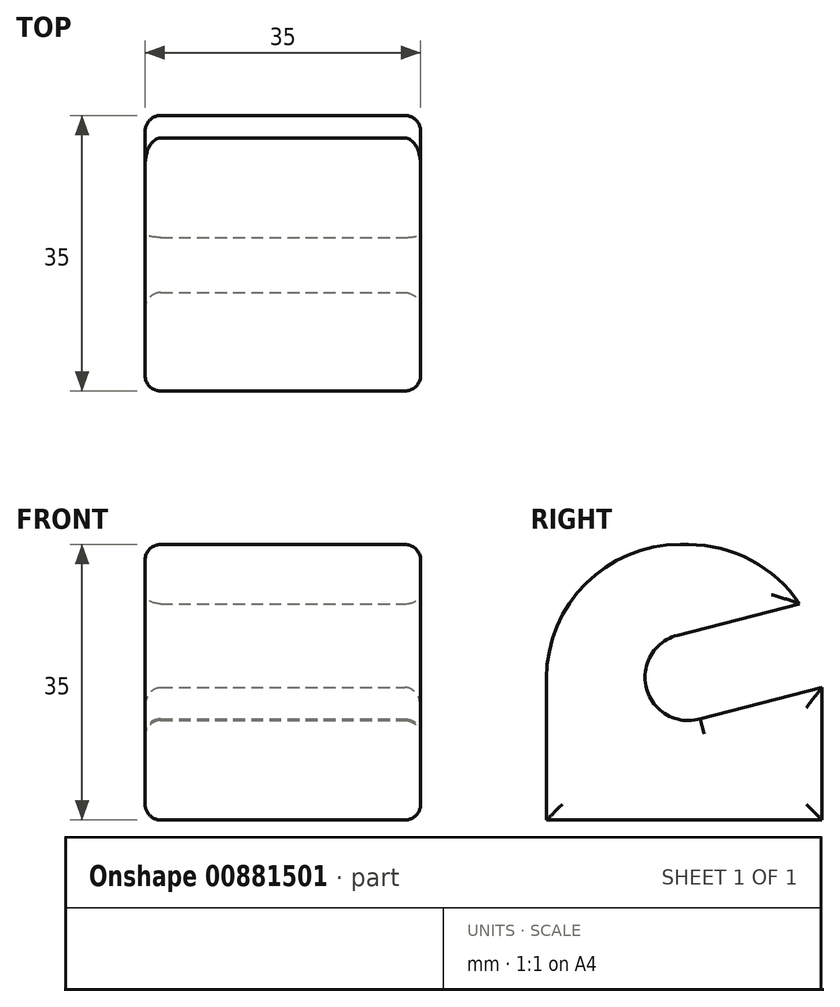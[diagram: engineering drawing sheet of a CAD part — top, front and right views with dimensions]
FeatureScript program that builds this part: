
annotation { "Feature Type Name" : "Feature", "Feature Type Description" : "" }
export const myFeature = defineFeature(function(context is Context, id is Id, definition is map)
    precondition{}
    {
        {
            var Q0;
            Q0=qCreatedBy(makeId("Top.planeOp"),FACE);
            var sketch = newSketch(context, id + "F0", { "sketchPlane" : qUnion([Q0])});
            skLineSegment(sketch, "E0.bottom", {"start": v(17.5, 17.5) * mm, "end": v(-17.5, 17.5) * mm});
            skLineSegment(sketch, "E0.top", {"start": v(17.5, -17.5) * mm, "end": v(-17.5, -17.5) * mm});
            skLineSegment(sketch, "E0.left", {"start": v(17.5, 17.5) * mm, "end": v(17.5, -17.5) * mm});
            skLineSegment(sketch, "E0.right", {"start": v(-17.5, 17.5) * mm, "end": v(-17.5, -17.5) * mm});
            skPoint(sketch, "E0.middle", {"position": v(0, 0) * mm});
            skPoint(sketch, "E1.visualSharp", {"position": v(-17.5, 17.5) * mm});
            skLineSegment(sketch, "E1.filletArc", {"start": v(-17.5, 17.5) * mm, "end": v(-17.5, 17.5) * mm});
            skPoint(sketch, "E2.visualSharp", {"position": v(17.5, 17.5) * mm});
            skLineSegment(sketch, "E2.filletArc", {"start": v(17.5, 17.5) * mm, "end": v(17.5, 17.5) * mm});
            skPoint(sketch, "E3.visualSharp", {"position": v(17.5, -17.5) * mm});
            skLineSegment(sketch, "E3.filletArc", {"start": v(17.5, -17.5) * mm, "end": v(17.5, -17.5) * mm});
            skPoint(sketch, "E4.visualSharp", {"position": v(-17.5, -17.5) * mm});
            skLineSegment(sketch, "E4.filletArc", {"start": v(-17.5, -17.5) * mm, "end": v(-17.5, -17.5) * mm});
            skSolve(sketch);
        }
        {
            var Q0;
            Q0=makeQuery(id+"F0.imprint","IMPRINT",FACE,{"disambiguationData":[TD([[makeQuery(id+"F0.imprint","IMPRINT",EDGE,{"derivedFrom":sQuery(id+"F0.wireOp",EDGE,"E0.bottom")}),1.0]])]});
            extrude(context, id + "F1", {"entities" : qUnion([Q0]), "depth" : 35 * mm, "offsetDistance" : 25 * mm});
        }
        {
            var Q0;
            Q0=makeQuery(id+"F1.opExtrude","CAP_EDGE",EDGE,{"disambiguationData":[OSD([sQuery(id+"F0.wireOp",EDGE,"E0.top")])],"isStart":false});
            var Q1;
            Q1=makeQuery(id+"F1.opExtrude","CAP_EDGE",EDGE,{"disambiguationData":[OSD([sQuery(id+"F0.wireOp",EDGE,"E0.bottom")])],"isStart":false});
            fillet(context, id + "F2", {"entities" : qUnion([Q0, Q1]), "radius" : 17 * mm, "allowEdgeOverflow" : false});
        }
        {
            var Q0;
            Q0=makeQuery(id+"F1.opExtrude","SWEPT_FACE",FACE,{"disambiguationData":[OSD([sQuery(id+"F0.wireOp",EDGE,"E0.left")])]});
            var sketch = newSketch(context, id + "F3", { "sketchPlane" : qUnion([Q0])});
            skSolve(sketch);
        }
        {
            var Q0;
            {var subQ0=sQuery(id+"F0.wireOp",EDGE,"E0.left");Q0=makeQuery(id+"F3.imprint","IMPRINT",FACE,{"disambiguationData":[TD([[makeQuery(id+"F3.imprint","IMPRINT",EDGE,{"derivedFrom":makeQuery(id+"F1.opExtrude","CAP_EDGE",EDGE,{"disambiguationData":[OSD([subQ0])],"isStart":true})}),-1.0]])]});}
            var sketch = newSketch(context, id + "F4", { "sketchPlane" : qUnion([Q0])});
            skLineSegment(sketch, "E5", {"start": v(14.62, 27.47) * mm, "end": v(-0.87, 23.47) * mm});
            skLineSegment(sketch, "E6", {"start": v(17.5, 16.85) * mm, "end": v(2, 12.85) * mm});
            skArc(sketch, "E7", {"start": v(-0.87, 23.47) * mm, "mid": v(-4.8, 16.7) * mm, "end": v(2, 12.85) * mm});
            skSolve(sketch);
        }
        {
            var Q0;
            Q0 = qSketchRegion(id + "F3", true);
            var Q1;
            {var subQ6=sQuery(id+"F4.wireOp",EDGE,"E5");Q1=makeQuery(id+"F4.imprint","IMPRINT",FACE,{"disambiguationData":[TD([[makeQuery(id+"F4.imprint","IMPRINT",EDGE,{"derivedFrom":subQ6}),1.0]])]});}
            extrude(context, id + "F5", {"entities" : qUnion([Q0, Q1]), "operationType" : NewBodyOperationType.REMOVE, "endBound" : BoundingType.THROUGH_ALL, "oppositeDirection" : true, "depth" : 25 * mm, "offsetDistance" : 25 * mm});
        }
        {
            var Q0;
            Q0=makeQuery(id+"F1.opExtrude","SWEPT_FACE",FACE,{"disambiguationData":[OSD([sQuery(id+"F0.wireOp",EDGE,"E0.left")])]});
            var Q1;
            Q1=makeQuery(id+"F1.opExtrude","SWEPT_FACE",FACE,{"disambiguationData":[OSD([sQuery(id+"F0.wireOp",EDGE,"E0.right")])]});
            var Q2;
            Q2=makeQuery(id+"F5.boolean.opBoolean","COPY",EDGE,{"derivedFrom":makeQuery(id+"F5.opExtrude","SWEPT_EDGE",EDGE,{"disambiguationData":[OSD([sQuery(id+"F0.wireOp",EDGE,"E0.bottom"),sQuery(id+"F0.wireOp",EDGE,"E0.left"),sQuery(id+"F4.wireOp",EDGE,"E5")])]})});
            var Q3;
            Q3=makeQuery(id+"F5.boolean.opBoolean","COPY",EDGE,{"derivedFrom":makeQuery(id+"F5.opExtrude","SWEPT_EDGE",EDGE,{"disambiguationData":[OSD([sQuery(id+"F0.wireOp",EDGE,"E0.bottom"),sQuery(id+"F0.wireOp",EDGE,"E0.left"),sQuery(id+"F4.wireOp",EDGE,"E6")])]})});
            fillet(context, id + "F6", {"entities" : qUnion([Q0, Q1, Q2, Q3]), "radius" : 2 * mm, "tangentPropagation" : true, "allowEdgeOverflow" : false});
        }
    });
